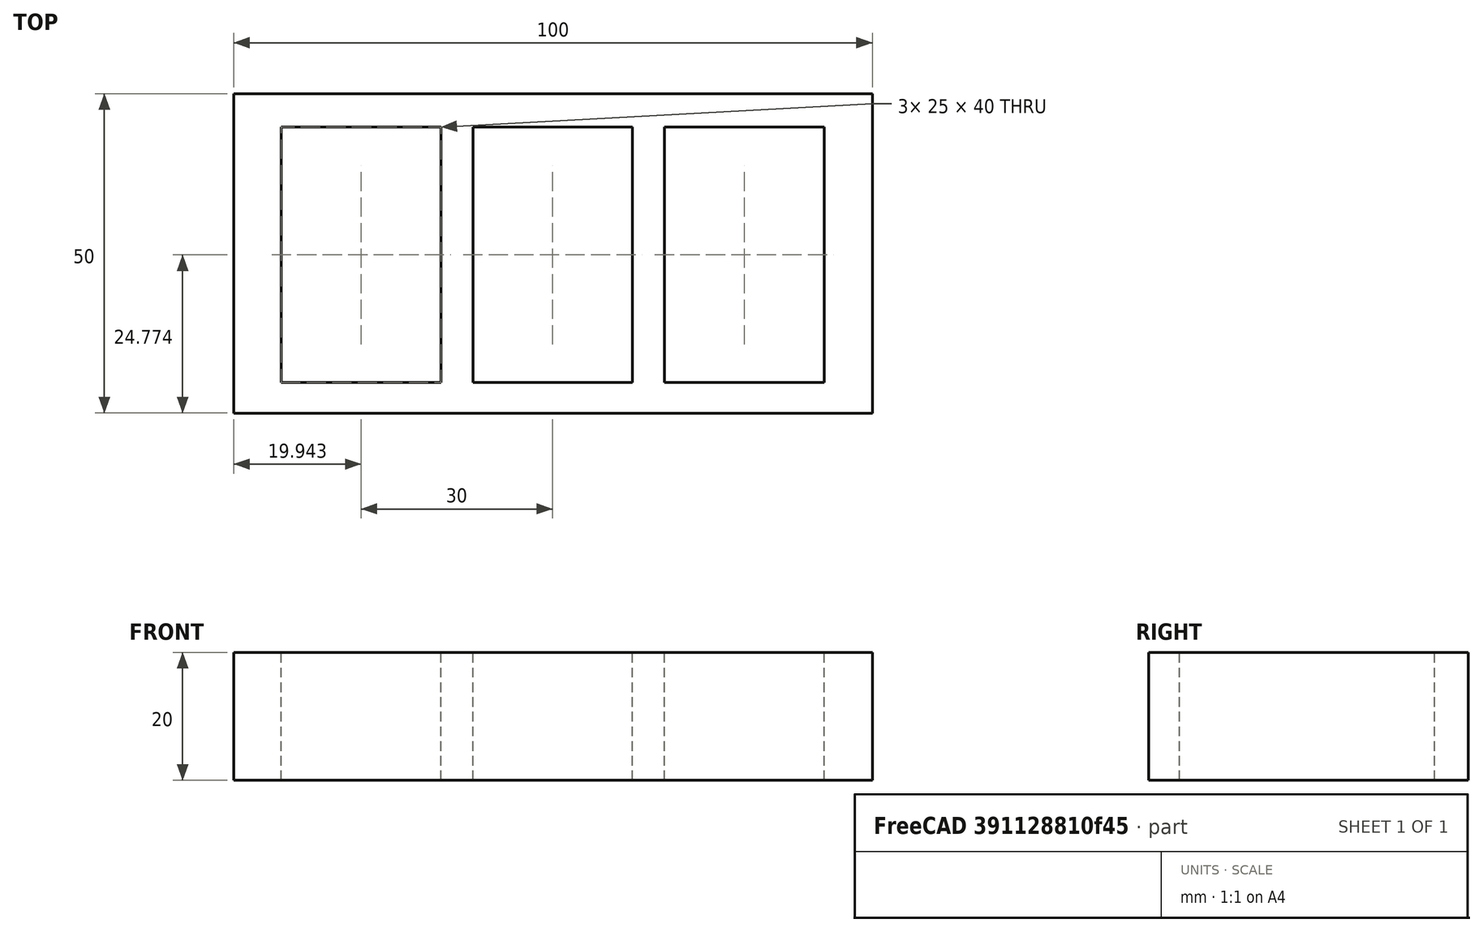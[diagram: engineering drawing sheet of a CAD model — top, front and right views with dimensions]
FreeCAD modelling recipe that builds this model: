
FCSTD DOCUMENT  (FreeCAD 0.20R29603 (Git))
Label: ielkadi_rete_3
License: All rights reserved
LicenseURL: http://en.wikipedia.org/wiki/All_rights_reserved
objects: Sketcher::SketchObject×2, PartDesign::Pad×1, PartDesign::Body×1
note: 5 computed .brp shape members not serialized (recipe doc carries the construction recipe); baked Part::Feature solids carry a one-line shape summary decoded from their .brp

FEATURE [Sketcher::SketchObject] Sketch
  FullyConstrained = false
  MapMode = 5
  Support = -> [XY_Plane]
  sketch-geometry (16):
    g0: LineSegment StartX=-49.7356 StartY=25.1967 StartZ=0 EndX=50.2644 EndY=25.1967 EndZ=0
    g1: LineSegment StartX=50.2644 StartY=25.1967 StartZ=0 EndX=50.2644 EndY=-24.8033 EndZ=0
    g2: LineSegment StartX=50.2644 StartY=-24.8033 StartZ=0 EndX=-49.7356 EndY=-24.8033 EndZ=0
    g3: LineSegment StartX=-49.7356 StartY=-24.8033 StartZ=0 EndX=-49.7356 EndY=25.1967 EndZ=0
    g4: LineSegment StartX=-42.2968 StartY=19.9743 StartZ=0 EndX=-17.2968 EndY=19.9743 EndZ=0
    g5: LineSegment StartX=-17.2968 StartY=19.9743 StartZ=0 EndX=-17.2968 EndY=-20.0257 EndZ=0
    g6: LineSegment StartX=-17.2968 StartY=-20.0257 StartZ=0 EndX=-42.2968 EndY=-20.0257 EndZ=0
    g7: LineSegment StartX=-42.2968 StartY=-20.0257 StartZ=0 EndX=-42.2968 EndY=19.9743 EndZ=0
    g8: LineSegment StartX=-12.2968 StartY=19.9743 StartZ=0 EndX=12.7032 EndY=19.9743 EndZ=0
    g9: LineSegment StartX=12.7032 StartY=19.9743 StartZ=0 EndX=12.7032 EndY=-20.0257 EndZ=0
    g10: LineSegment StartX=12.7032 StartY=-20.0257 StartZ=0 EndX=-12.2968 EndY=-20.0257 EndZ=0
    g11: LineSegment StartX=-12.2968 StartY=-20.0257 StartZ=0 EndX=-12.2968 EndY=19.9743 EndZ=0
    g12: LineSegment StartX=17.7032 StartY=19.9743 StartZ=0 EndX=42.7032 EndY=19.9743 EndZ=0
    g13: LineSegment StartX=42.7032 StartY=19.9743 StartZ=0 EndX=42.7032 EndY=-20.0257 EndZ=0
    g14: LineSegment StartX=42.7032 StartY=-20.0257 StartZ=0 EndX=17.7032 EndY=-20.0257 EndZ=0
    g15: LineSegment StartX=17.7032 StartY=-20.0257 StartZ=0 EndX=17.7032 EndY=19.9743 EndZ=0
  constraints (42):
    c: Coincident(g0,g1)
    c: Coincident(g1,g2)
    c: Coincident(g2,g3)
    c: Coincident(g3,g0)
    c: Horizontal(g0)
    c: Horizontal(g2)
    c: Vertical(g1)
    c: Vertical(g3)
    c: DistanceY(g2,g0) = 50
    c: DistanceX(g0,g0) = 100
    c: Coincident(g4,g5)
    c: Coincident(g5,g6)
    c: Coincident(g6,g7)
    c: Coincident(g7,g4)
    c: Horizontal(g4)
    c: Horizontal(g6)
    c: Vertical(g5)
    c: Vertical(g7)
    c: DistanceX(g4,g4) = 25
    c: DistanceY(g7,g7) = 40
    c: DistanceX(g4,g8) = 5
    c: Coincident(g8,g9)
    c: Coincident(g9,g10)
    c: Coincident(g10,g11)
    c: Coincident(g11,g8)
    c: Horizontal(g8)
    c: Horizontal(g10)
    c: Vertical(g9)
    c: Vertical(g11)
    c: DistanceX(g8,g8) = 25
    c: DistanceY(g11,g11) = 40
    c: DistanceX(g8,g12) = 5
    c: Coincident(g12,g13)
    c: Coincident(g13,g14)
    c: Coincident(g14,g15)
    c: Coincident(g15,g12)
    c: Horizontal(g12)
    c: Horizontal(g14)
    c: Vertical(g13)
    c: Vertical(g15)
    c: DistanceX(g12,g12) = 25
    c: DistanceY(g15,g15) = 40
FEATURE [PartDesign::Pad] Pad
  Direction = (0,0,1)
  Length = 20
  Length2 = 10
  Profile = -> Sketch
  ReferenceAxis = -> Sketch [N_Axis]
  Type = 0
FEATURE [Sketcher::SketchObject] Sketch001
  FullyConstrained = false
  MapMode = 5
  Placement = pos=(-49.7356,0,0) rot=(0.57735,-0.57735,-0.57735;2.0944rad)
  Support = -> [Pad]
  sketch-geometry (1):
    g0: Circle CenterX=0 CenterY=10.0394 CenterZ=0 NormalX=0 NormalY=0 NormalZ=1 AngleXU=0 Radius=6.70057
  constraints (1):
    c: PointOnObject(g0,g-2)
FEATURE [PartDesign::Body] Body
  Group = -> [Sketch,Pad,Sketch001]
  Origin = -> Origin
  Tip = -> Pad
